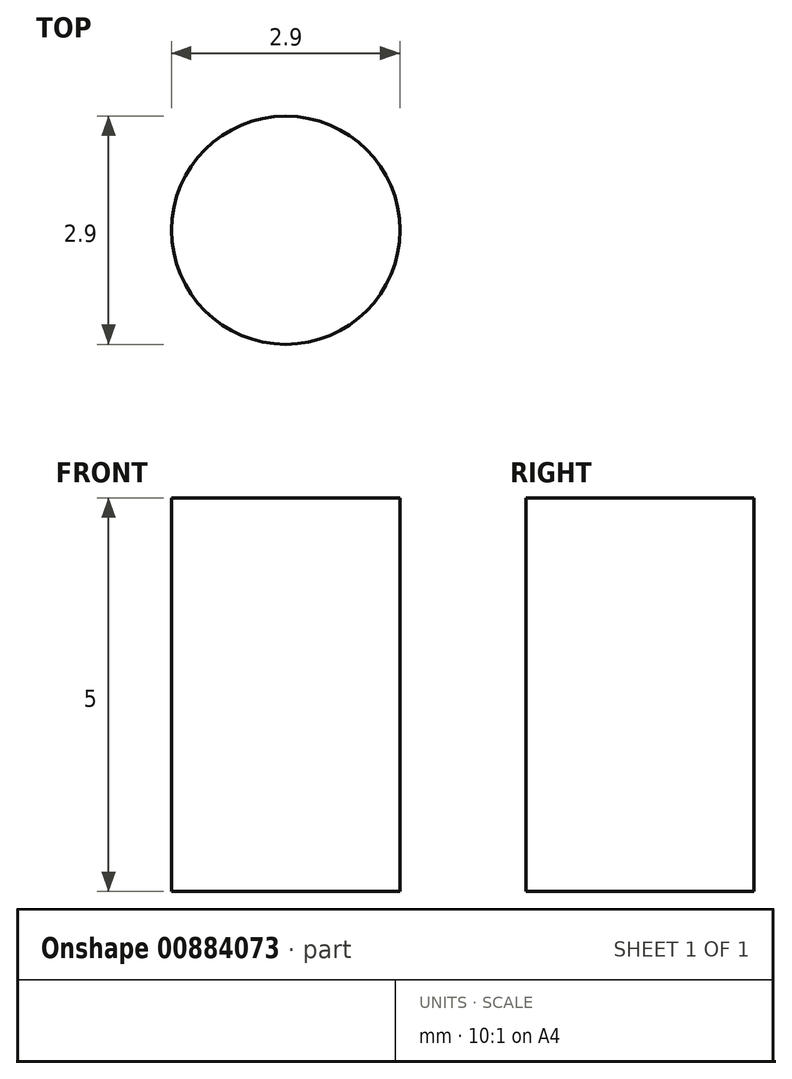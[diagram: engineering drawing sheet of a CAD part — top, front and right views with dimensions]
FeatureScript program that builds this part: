
annotation { "Feature Type Name" : "Feature", "Feature Type Description" : "" }
export const myFeature = defineFeature(function(context is Context, id is Id, definition is map)
    precondition{}
    {
        {
            var Q0;
            Q0=qCreatedBy(makeId("Top.planeOp"),FACE);
            var sketch = newSketch(context, id + "F0", { "sketchPlane" : qUnion([Q0])});
            skCircle(sketch, "E0", {"center": v(0, 0) * mm, "radius": 1.45 * mm});
            skSolve(sketch);
        }
        {
            var Q0;
            Q0=makeQuery(id+"F0.imprint","IMPRINT",FACE,{"disambiguationData":[TD([[makeQuery(id+"F0.imprint","IMPRINT",EDGE,{"derivedFrom":sQuery(id+"F0.wireOp",EDGE,"E0")}),1.0]])]});
            extrude(context, id + "F1", {"entities" : qUnion([Q0]), "depth" : 5 * mm, "offsetDistance" : 25 * mm});
        }
    });
